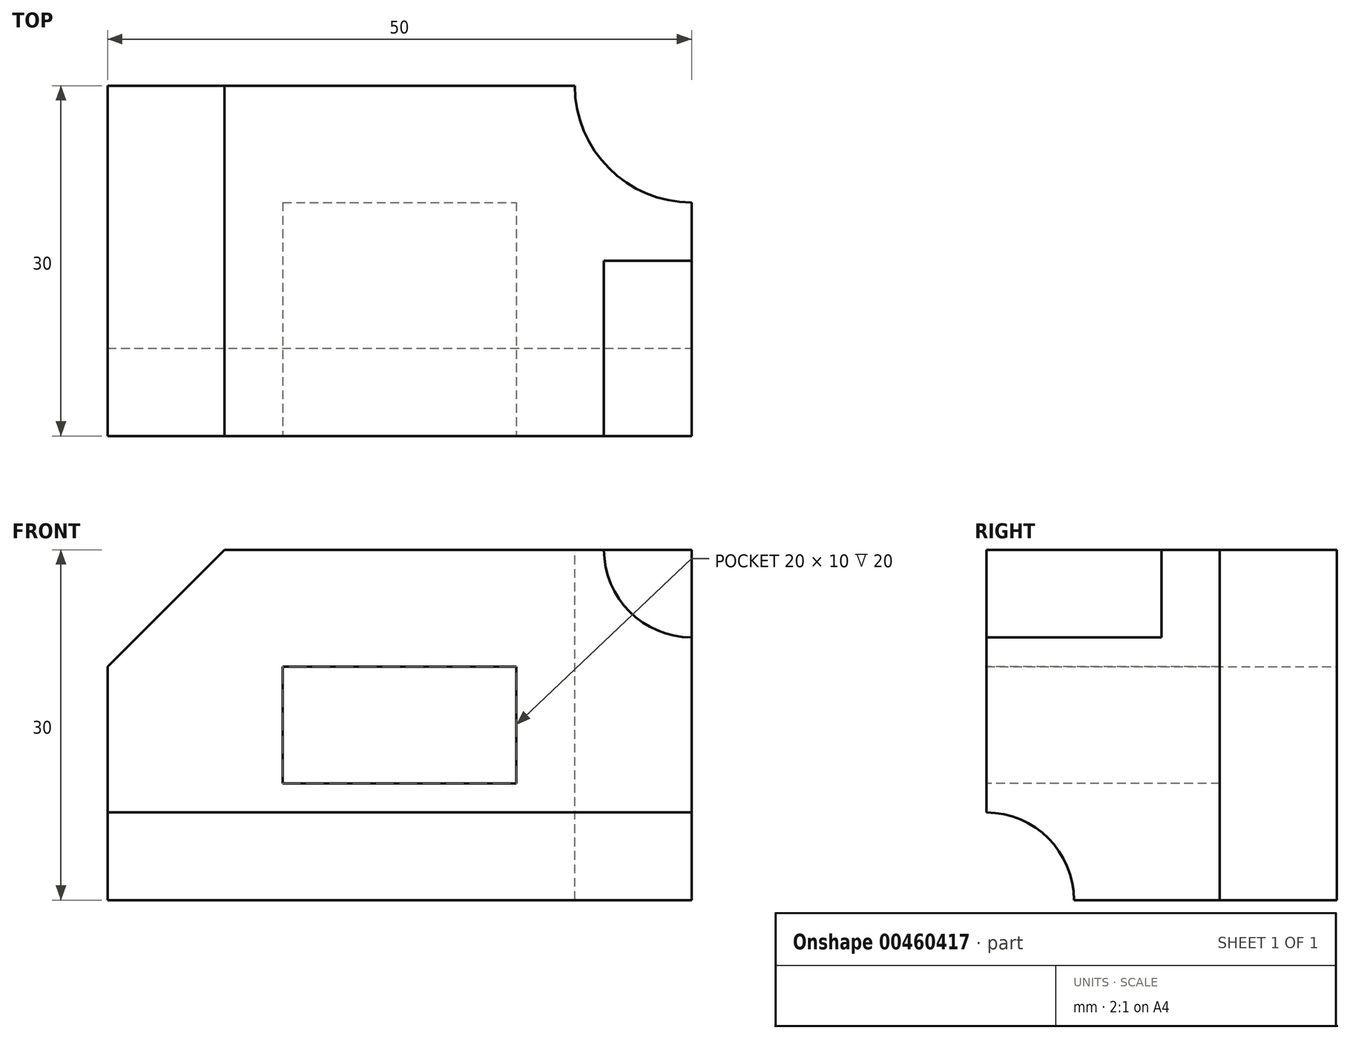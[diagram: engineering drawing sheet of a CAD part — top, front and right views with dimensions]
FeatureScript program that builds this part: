
annotation { "Feature Type Name" : "Feature", "Feature Type Description" : "" }
export const myFeature = defineFeature(function(context is Context, id is Id, definition is map)
    precondition{}
    {
        {
            var Q0;
            Q0=qCreatedBy(makeId("Front.planeOp"),FACE);
            var sketch = newSketch(context, id + "F0", { "sketchPlane" : qUnion([Q0])});
            skLineSegment(sketch, "E0.bottom", {"start": v(0, 0) * mm, "end": v(-50, 0) * mm});
            skLineSegment(sketch, "E0.top", {"start": v(0, 30) * mm, "end": v(-50, 30) * mm});
            skLineSegment(sketch, "E0.left", {"start": v(0, 0) * mm, "end": v(0, 30) * mm});
            skLineSegment(sketch, "E0.right", {"start": v(-50, 0) * mm, "end": v(-50, 30) * mm});
            skSolve(sketch);
        }
        {
            var Q0;
            Q0=makeQuery(id+"F0.imprint","IMPRINT",FACE,{"disambiguationData":[TD([[makeQuery(id+"F0.imprint","IMPRINT",EDGE,{"derivedFrom":sQuery(id+"F0.wireOp",EDGE,"E0.bottom")}),-1.0]])]});
            extrude(context, id + "F1", {"entities" : qUnion([Q0]), "depth" : 30 * mm});
        }
        {
            var Q0;
            Q0=makeQuery(id+"F1.opExtrude","SWEPT_FACE",FACE,{"disambiguationData":[OSD([sQuery(id+"F0.wireOp",EDGE,"E0.left")])]});
            var sketch = newSketch(context, id + "F2", { "sketchPlane" : qUnion([Q0])});
            skCircle(sketch, "E1", {"center": v(-30, 0) * mm, "radius": 7.5 * mm});
            skSolve(sketch);
        }
        {
            var Q0;
            {var subQ0=sQuery(id+"F2.wireOp",EDGE,"E1");var subQ1=sQuery(id+"F0.wireOp",EDGE,"E0.left");var subQ4=makeQuery(id+"F1.opExtrude","CAP_EDGE",EDGE,{"disambiguationData":[OSD([subQ1])],"isStart":false});var subQ5=makeQuery(id+"F2.imprint","INTERSECT",VERTEX,{"derivedFrom":[subQ4,subQ0]});Q0=makeQuery(id+"F2.imprint","IMPRINT",FACE,{"disambiguationData":[TD([[makeQuery(id+"F2.imprint","IMPRINT",EDGE,{"disambiguationData":[TD([[subQ5,1.0]])],"derivedFrom":subQ0}),1.0]])]});}
            extrude(context, id + "F3", {"entities" : qUnion([Q0]), "operationType" : NewBodyOperationType.REMOVE, "endBound" : BoundingType.UP_TO_NEXT, "oppositeDirection" : true, "depth" : 25 * mm});
        }
        {
            var Q0;
            Q0=makeQuery(id+"F1.opExtrude","SWEPT_FACE",FACE,{"disambiguationData":[OSD([sQuery(id+"F0.wireOp",EDGE,"E0.top")])]});
            var sketch = newSketch(context, id + "F4", { "sketchPlane" : qUnion([Q0])});
            skCircle(sketch, "E2", {"center": v(0, 0) * mm, "radius": 10 * mm});
            skSolve(sketch);
        }
        {
            var Q0;
            {var subQ0=sQuery(id+"F4.wireOp",EDGE,"E2");var subQ1=sQuery(id+"F0.wireOp",EDGE,"E0.top");var subQ4=makeQuery(id+"F1.opExtrude","CAP_EDGE",EDGE,{"disambiguationData":[OSD([subQ1])],"isStart":true});var subQ5=makeQuery(id+"F4.imprint","INTERSECT",VERTEX,{"derivedFrom":[subQ4,subQ0]});Q0=makeQuery(id+"F4.imprint","IMPRINT",FACE,{"disambiguationData":[TD([[makeQuery(id+"F4.imprint","IMPRINT",EDGE,{"disambiguationData":[TD([[subQ5,-1.0]])],"derivedFrom":subQ0}),1.0]])]});}
            extrude(context, id + "F5", {"entities" : qUnion([Q0]), "operationType" : NewBodyOperationType.REMOVE, "endBound" : BoundingType.UP_TO_NEXT, "oppositeDirection" : true, "depth" : 25 * mm});
        }
        {
            var Q0;
            Q0=makeQuery(id+"F1.opExtrude","CAP_FACE",FACE,{"disambiguationData":[OSD([sQuery(id+"F0.wireOp",EDGE,"E0.bottom"),sQuery(id+"F0.wireOp",EDGE,"E0.top"),sQuery(id+"F0.wireOp",EDGE,"E0.left"),sQuery(id+"F0.wireOp",EDGE,"E0.right")])],"isStart":false});
            var sketch = newSketch(context, id + "F6", { "sketchPlane" : qUnion([Q0])});
            skCircle(sketch, "E3", {"center": v(0, 30) * mm, "radius": 7.5 * mm});
            skLineSegment(sketch, "E4.bottom", {"start": v(-35, 20) * mm, "end": v(-15, 20) * mm});
            skLineSegment(sketch, "E4.top", {"start": v(-35, 10) * mm, "end": v(-15, 10) * mm});
            skLineSegment(sketch, "E4.left", {"start": v(-35, 20) * mm, "end": v(-35, 10) * mm});
            skLineSegment(sketch, "E4.right", {"start": v(-15, 20) * mm, "end": v(-15, 10) * mm});
            skSolve(sketch);
        }
        {
            var Q0;
            {var subQ0=sQuery(id+"F6.wireOp",EDGE,"E3");var subQ1=makeQuery(id+"F1.opExtrude","CAP_EDGE",EDGE,{"disambiguationData":[OSD([sQuery(id+"F0.wireOp",EDGE,"E0.top")])],"isStart":false});var subQ2=makeQuery(id+"F6.imprint","INTERSECT",VERTEX,{"derivedFrom":[subQ1,subQ0]});Q0=makeQuery(id+"F6.imprint","IMPRINT",FACE,{"disambiguationData":[TD([[makeQuery(id+"F6.imprint","IMPRINT",EDGE,{"disambiguationData":[TD([[subQ2,-1.0]])],"derivedFrom":subQ0}),1.0]])]});}
            extrude(context, id + "F7", {"entities" : qUnion([Q0]), "operationType" : NewBodyOperationType.REMOVE, "oppositeDirection" : true, "depth" : 15 * mm});
        }
        {
            var Q0;
            Q0=makeQuery(id+"F6.imprint","IMPRINT",FACE,{"disambiguationData":[TD([[makeQuery(id+"F6.imprint","IMPRINT",EDGE,{"derivedFrom":sQuery(id+"F6.wireOp",EDGE,"E4.bottom")}),-1.0]])]});
            extrude(context, id + "F8", {"entities" : qUnion([Q0]), "operationType" : NewBodyOperationType.REMOVE, "oppositeDirection" : true, "depth" : 20 * mm});
        }
        {
            var Q0;
            Q0=makeQuery(id+"F1.opExtrude","SWEPT_EDGE",EDGE,{"disambiguationData":[OSD([sQuery(id+"F0.wireOp",EDGE,"E0.top"),sQuery(id+"F0.wireOp",EDGE,"E0.right")])]});
            chamfer(context, id + "F9", {"entities" : qUnion([Q0]), "width" : 10 * mm, "tangentPropagation" : true});
        }
    });
